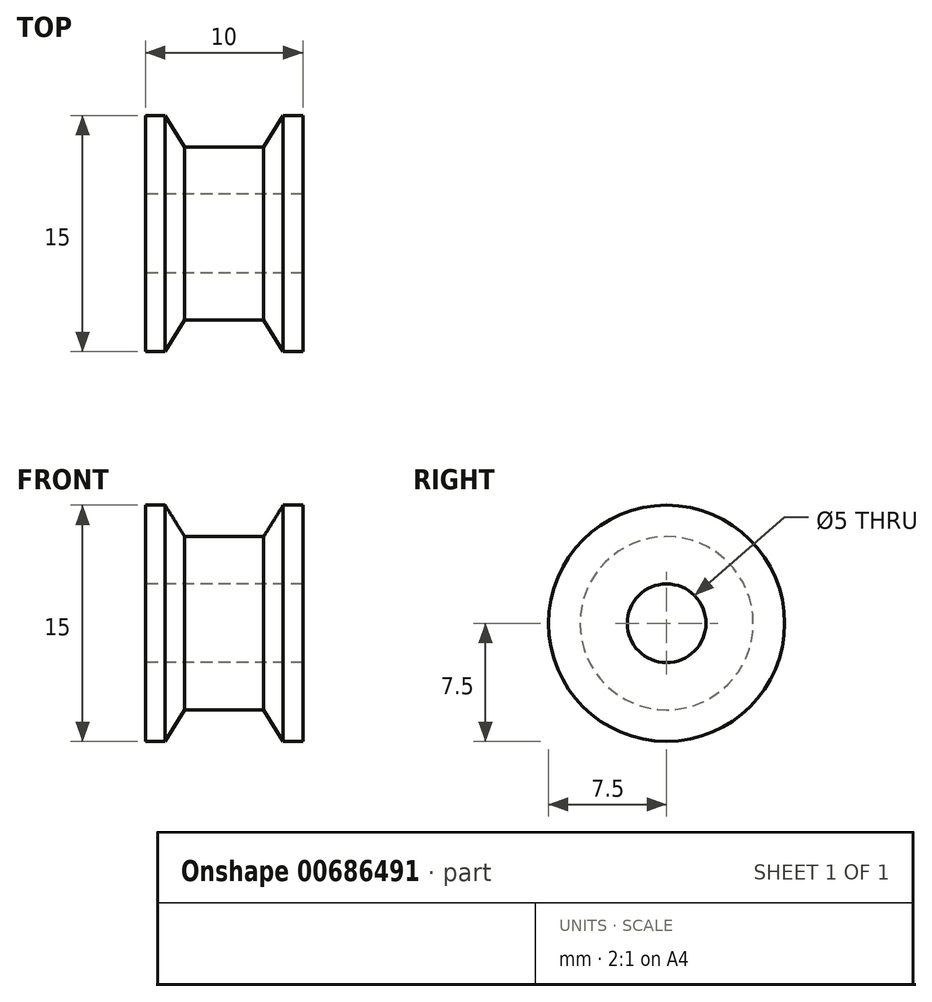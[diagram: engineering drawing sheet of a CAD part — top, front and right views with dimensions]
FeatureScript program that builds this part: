
annotation { "Feature Type Name" : "Feature", "Feature Type Description" : "" }
export const myFeature = defineFeature(function(context is Context, id is Id, definition is map)
    precondition{}
    {
        {
            var Q0;
            Q0=qCreatedBy(makeId("Front.planeOp"),FACE);
            var sketch = newSketch(context, id + "F0", { "sketchPlane" : qUnion([Q0])});
            skLineSegment(sketch, "E0.bottom", {"start": v(-5, 0) * mm, "end": v(5, 0) * mm});
            skLineSegment(sketch, "E0.left", {"start": v(-5, 0) * mm, "end": v(-5, 5) * mm});
            skLineSegment(sketch, "E0.right", {"start": v(5, 0) * mm, "end": v(5, 5) * mm});
            skLineSegment(sketch, "E1", {"start": v(-6.73, -2.5) * mm, "end": v(10.13, -2.5) * mm});
            skLineSegment(sketch, "E2", {"start": v(-2.5, 3) * mm, "end": v(2.5, 3) * mm});
            skLineSegment(sketch, "E3", {"start": v(-5, 5) * mm, "end": v(-3.75, 5) * mm});
            skLineSegment(sketch, "E4", {"start": v(-3.75, 5) * mm, "end": v(-2.5, 3) * mm});
            skLineSegment(sketch, "E5", {"start": v(2.5, 3) * mm, "end": v(3.75, 5) * mm});
            skLineSegment(sketch, "E6", {"start": v(3.75, 5) * mm, "end": v(5, 5) * mm});
            skSolve(sketch);
        }
        {
            var Q0;
            Q0 = qSketchRegion(id + "F0", true);
            var Q1;
            Q1=sQuery(id+"F0.wireOp",EDGE,"E1");
            revolve(context, id + "F1", {"entities" : qUnion([Q0]), "axis" : qUnion([Q1]), "revolveType" : RevolveType.FULL});
        }
    });
